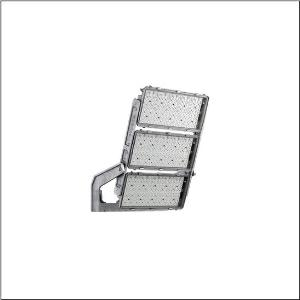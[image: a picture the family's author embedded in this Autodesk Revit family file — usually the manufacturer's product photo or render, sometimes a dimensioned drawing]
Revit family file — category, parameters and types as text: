
# Revit family: floodlight_fl_11_maxi_pro_remote___pl52_5xa779427d01aa_0793
name_source: partatom
category: Lighting Fixtures
units: mm (PartAtom-declared; Revit-internal decimal feet)

## family parameters
Cut with Voids When Loaded = No
Host = Face
Light Source = No
Part Type = Normal
Room Calculation Point = No
Round Connector Dimension = Use Diameter
Shared = No

## types (1)
- --- (1 x LED, 173640 lm, 1425.5 W, 5000K)
    Apparent Load = 1425 VA
    CIE Flux Codes = 24 55 98 100 100
    Color Rendering = 70
    Color Temperature = 5000K
    Default Elevation = 1800 mm
    Description = Floodlight FL 11  maxi  pro Remote floodlight; light control with lens of PMMA; cover panel of toughened safety glass, transparent; light distribution: PL52, asymmetric direct distribution, LEDcolour temperature: 5000K, rated luminous flux: 173.640lm, colour rendering: CRI > 70, light colour: 750; luminous efficacy: 122lm/W; brightness control: DALI 2 (1 DALI address); with terminal, 8-pole, max. 2.5mm², mains connection: 220..240V/380..400V AC, 50/60Hz, surge voltage resistance: line to ground: 10kV, ECG replaceable separately, LED unit replaceable without ESD environment, dustproof LED module, dimming range 10..100%, no afterglow with DALI off / DMX off command; 1426W floodlight with 3x LED unit of diecast aluminium, coated grey; length: 713mm / width: 651mm / height: 338mm; mounting bracket, of diecast aluminium, uncoated, natural, equipment: Power, protection rating (complete): IP66; insulation class (complete): insulation class I (protective earthing); certification: CE, ENEC, VDE; ball protection: ball impact resistance with accessories, impact resistance: IK07; rated ambient temperature 10°C, only for outdoor installations, permissible operating ambient temperature: -40..+30°C, permissible storage temperature: -40..+85°C; packaging unit: 1 piece

Light Distribution: PL52
    Height = 320 mm
    Lamp = 1 x LED
    Lamp Light Flux = 173640 lm
    Lamp Power = 1425.5 W
    Lamp count = 1
    Length = 1002 mm
    Luminous efficacy = 122 lm/W
    Manufacturer = Siteco
    ModVariant = No
    Model = 5XA779427D01AA
    Mounting Place = Ceiling
    Mounting Type = Surface mounted
    Number of Poles = 1
    OnlyDefault = Yes
    Power Factor = 1
    Product Name = Floodlight FL 11 maxi pro Remote | PL52
    Product group = floodlight | ceiling mounted
    ProductGroupID = 302
    Protection Class = Protection class I
    Protection Degree = IP 66
    RLX_Detail_Level = 1
    RLX_Emergency_Light_Flux = 0 lm
    RLX_Emergency_Type = 0
    RLX_Emergency_Type_DB = No
    RlxData = <blob elided: 52505 chars, md5=34f890de>
    Socket = socket
    Standby Power = 0 W
    System Light Flux = 173640 lm
    System Power = 1425 W
    Type Comments = factory setting: luminous flux: 100 % | dim-lin: 254 | 980 mA
    Type Image = l_1006784.jpg
    URL = http://relux.com
    VarID = @adj_066833
    Voltage = 0 V
    Weight = 0.00 kg
    Width = 655 mm

## geometry (parser evidence)
native form markers: Blend x4, Sweep x15
no freeform markers — native parametric forms only
